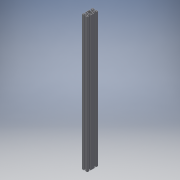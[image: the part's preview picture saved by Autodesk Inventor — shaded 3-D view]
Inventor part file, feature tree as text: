
AUTODESK INVENTOR PART (.ipt)
format: ipt  version: 2018 (Build 220112000, 112)  size: 636,416 bytes
history: native  units: mm
features: other x1, extrude x1, sketch x1
ambient origin geometry x8: Origin, YZ Plane, XZ Plane, XY Plane, X Axis, Y Axis, Z Axis, Center Point
bodies: Body1 (feature_tree)
feature tree (3):
  other  "Sólido1"
  extrude  "Extrusão1"  [1 undecoded]
  sketch  "Esboço1"  dims[d0=725.0mm d1=0.0mm]
note: 1 required parameter value undecoded (feature->parameter linkage not recoverable at this tier; creation-order binding heuristic only, values carry confidence <= 0.55)
